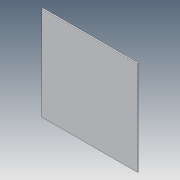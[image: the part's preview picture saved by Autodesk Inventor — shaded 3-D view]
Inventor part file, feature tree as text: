
AUTODESK INVENTOR PART (.ipt)
format: ipt  version: 2012 (Build 160160000, 160)  size: 1,934,336 bytes
history: native  units: in
note: dims shown in document units (in); Inventor stores cm internally (conversion verified against a paired STEP export)
features: other x2, sketch x2, extrude x1
ambient origin geometry x8: Origin, YZ Plane, XZ Plane, XY Plane, X Axis, Y Axis, Z Axis, Center Point
bodies: Solid1 (feature_tree)
feature tree (5):
  extrude  "Extrusion1"  Depth=48.0in
  other  "Decal1"
  sketch  "Sketch1"  dims[d0=47.0in d1=48.0in]
  sketch  "Sketch2"  dims[d2=0.5in d3=0.0in d24=3.0in d32=3.0in d38=87.8249in d39=18.5in]
  other  "Image1"
